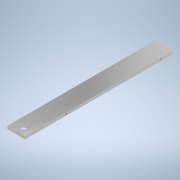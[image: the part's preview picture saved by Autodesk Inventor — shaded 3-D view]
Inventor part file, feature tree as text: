
AUTODESK INVENTOR PART (.ipt)
format: ipt  version: 2022 (Build 260153000, 153)  size: 125,952 bytes
history: native  units: mm
features: sketch x4, hole x3, other x1, extrude x1
ambient origin geometry x8: Origin, YZ Plane, XZ Plane, XY Plane, X Axis, Y Axis, Z Axis, Center Point
bodies: Body1 (feature_tree)
feature tree (9):
  other  "ソリッド1"
  extrude  "押し出し1"  Depth=250.0mm
  hole  "穴1"  [1 undecoded]
  hole  "穴2"  [1 undecoded]
  hole  "穴3"  [1 undecoded]
  sketch  "スケッチ1"
  sketch  "スケッチ2"
  sketch  "スケッチ3"
  sketch  "スケッチ4"
note: 3 required parameter values undecoded (feature->parameter linkage not recoverable at this tier; creation-order binding heuristic only, values carry confidence <= 0.55)
